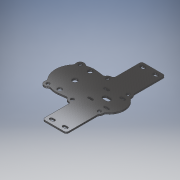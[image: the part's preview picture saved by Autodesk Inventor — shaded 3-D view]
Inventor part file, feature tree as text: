
AUTODESK INVENTOR PART (.ipt)
format: ipt  version: 2017 (Build 210142000, 142)  size: 373,248 bytes
history: native  units: mm
features: extrude x6, sketch x5, fillet x2, mirror x2, other x1, plane x1
ambient origin geometry x8: Origin, YZ Plane, XZ Plane, XY Plane, X Axis, Y Axis, Z Axis, Center Point
bodies: Body1 (feature_tree)
feature tree (17):
  other  "Sólido1"
  extrude  "Extrusión1"  Depth=88.9mm
  plane  "Plano de trabajo1"
  extrude  "Extrusión3"  Depth=22.225mm
  fillet  "Empalme5"  Radius=22.225mm
  mirror  "Simetría1"
  extrude  "Extrusión2"  Depth=22.225mm
  fillet  "Empalme6"  Radius=22.225mm
  extrude  "Extrusión5"  Depth=22.225mm
  extrude  "Extrusión6"  Depth=8.73125mm
  extrude  "Extrusión7"  Depth=8.73125mm
  mirror  "Simetría2"
  sketch  "Boceto1"  dims[d0=114.3mm d1=88.9mm]
  sketch  "Boceto2"  dims[d2=203.2mm d3=22.225mm d4=22.225mm]
  sketch  "Boceto5"  dims[d7=22.225mm d8=22.225mm d11=22.225mm]
  sketch  "Boceto6"  dims[d13=0.0mm d14=22.225mm]
  sketch  "Boceto7"  dims[d16=4.445mm d17=0.0mm d18=9.525mm d19=9.525mm d20=9.525mm d21=9.525mm d22=9.525mm d23=9.525mm d24=25.4mm d25=0.0mm d27=50.8mm d28=4.445mm d29=4.445mm d30=69.85mm d31=4.445mm d32=146.05mm d33=69.85mm d34=0.0mm d35=31.75mm d36=31.75mm d37=44.45mm d38=44.45mm d39=12.7mm d40=12.7mm d56=6.35mm d57=6.35mm d58=14.2875mm d59=45.0mm d60=45.0mm d61=12.7mm d62=12.7mm d63=25.4mm d64=0.0mm d65=12.7mm d66=0.0mm d67=93.4212mm d68=12.7mm d69=12.7mm d70=5.159375mm d71=5.159375mm d72=47.5mm d73=47.5mm d74=23.75mm d75=23.75mm d76=5.55625mm d77=5.55625mm d78=5.159375mm d79=5.159375mm d80=0.0mm d81=5.55625mm d82=5.55625mm d83=5.159375mm d84=5.159375mm d85=0.0mm d86=0.0mm d87=5.55625mm d88=5.55625mm d89=5.159375mm d90=5.159375mm d91=0.0mm d92=5.55625mm d93=5.55625mm d94=5.159375mm d95=5.159375mm d96=0.0mm d97=25.4mm d98=0.0mm d99=8.73125mm d101=15.875mm d104=8.73125mm d105=8.73125mm d106=12.7mm d107=0.0mm d108=0.0mm d110=3.373438mm d111=3.373438mm d112=8.73125mm d113=12.7mm d114=15.875mm d115=8.73125mm d116=8.73125mm d117=0.0mm d118=0.0mm d119=3.373438mm d120=3.373438mm d121=25.4mm d122=0.0mm]
